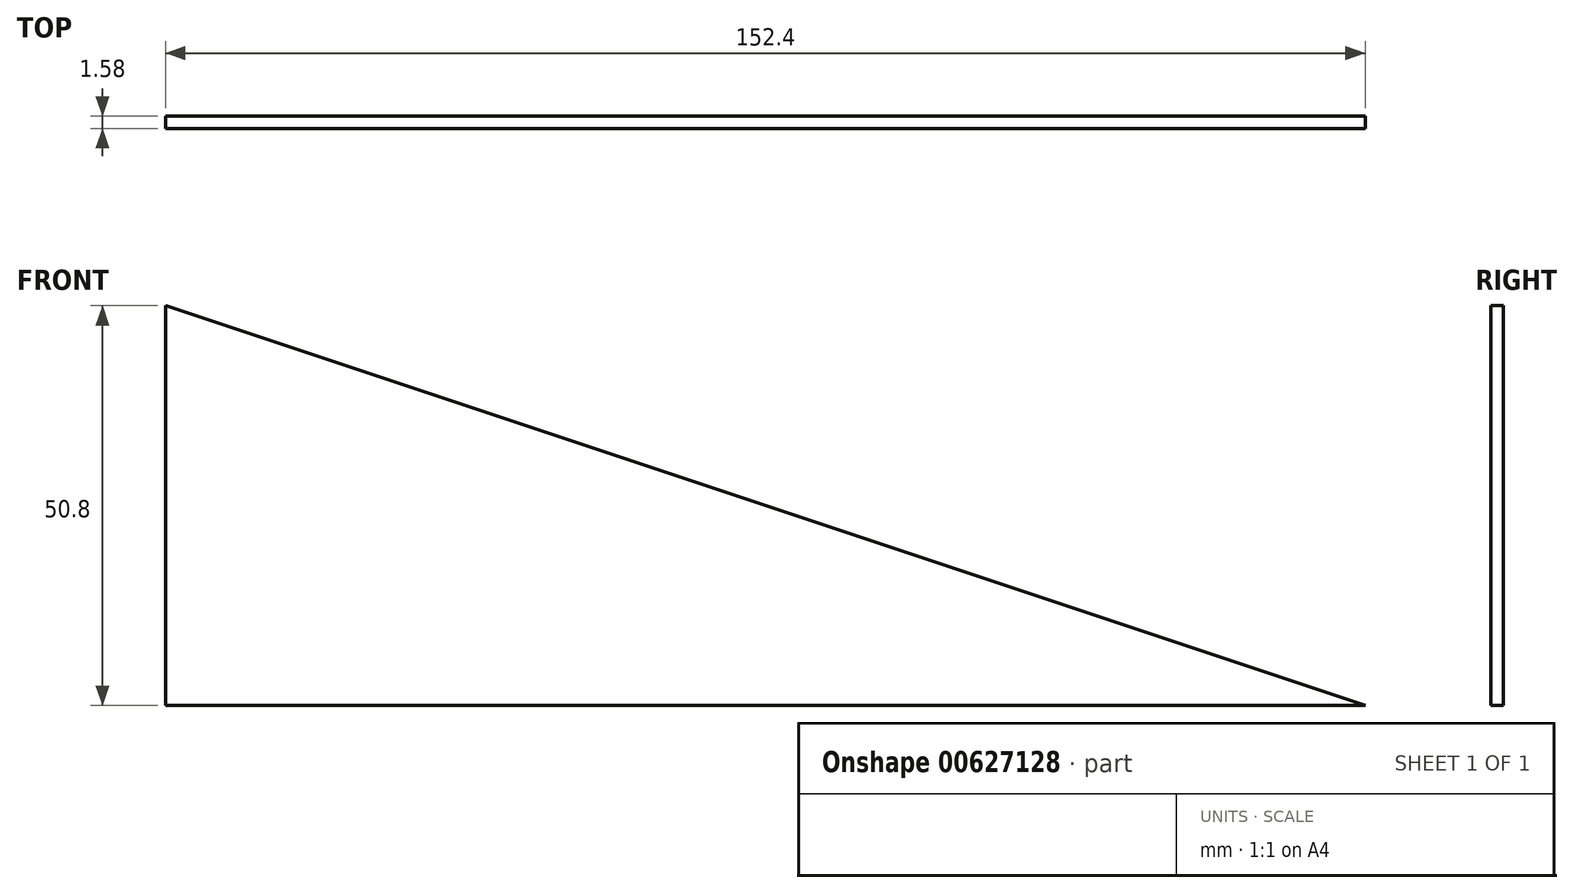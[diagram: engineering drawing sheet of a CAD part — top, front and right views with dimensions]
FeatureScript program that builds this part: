
annotation { "Feature Type Name" : "Feature", "Feature Type Description" : "" }
export const myFeature = defineFeature(function(context is Context, id is Id, definition is map)
    precondition{}
    {
        {
            var Q0;
            Q0=qCreatedBy(makeId("Front.planeOp"),FACE);
            var sketch = newSketch(context, id + "F0", { "sketchPlane" : qUnion([Q0])});
            skLineSegment(sketch, "E0.top", {"start": v(76.2, -25.4) * mm, "end": v(-76.2, -25.4) * mm});
            skLineSegment(sketch, "E0.right", {"start": v(-76.2, 25.4) * mm, "end": v(-76.2, -25.4) * mm});
            skPoint(sketch, "E0.middle", {"position": v(0, 0) * mm});
            skLineSegment(sketch, "E1", {"start": v(-76.2, 25.4) * mm, "end": v(76.2, -25.4) * mm});
            skPoint(sketch, "E0.left.start.orphan", {"position": v(76.2, 25.4) * mm});
            skSolve(sketch);
        }
        {
            var Q0;
            Q0=makeQuery(id+"F0.imprint","IMPRINT",FACE,{"disambiguationData":[TD([[makeQuery(id+"F0.imprint","IMPRINT",EDGE,{"derivedFrom":sQuery(id+"F0.wireOp",EDGE,"E0.top")}),-1.0]])]});
            extrude(context, id + "F1", {"entities" : qUnion([Q0]), "endBound" : BoundingType.SYMMETRIC, "depth" : 1.59 * mm, "offsetDistance" : 25.4 * mm});
        }
    });
